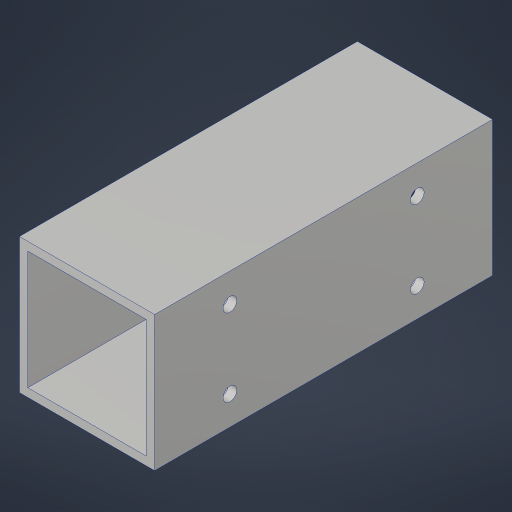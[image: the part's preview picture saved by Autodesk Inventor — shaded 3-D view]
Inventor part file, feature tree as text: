
AUTODESK INVENTOR PART (.ipt)
format: ipt  version: 2023.4 (Build 274418000, 418)  size: 167,424 bytes
history: native  units: in
note: dims shown in document units (in); Inventor stores cm internally (conversion verified against a paired STEP export)
features: extrude x1, hole x1, sketch x1, projected_geometry x1
ambient origin geometry x8: Origin, YZ Plane, XZ Plane, XY Plane, X Axis, Y Axis, Z Axis, Center Point
bodies: Solid1 (feature_tree)
feature tree (4):
  extrude  "Extrusion1"  Depth=3.0in
  hole  "Hole1"  [1 undecoded]
  sketch  "Sketch2"  dims[d4=0.0in d5=3.0in d6=3.1496in d8=360.0deg d10=0.201in d11=0.75in d12=0.385in d13=0.25in d14=0.5635in d15=1.0in d16=0.8108in]
  projected_geometry  "Project Cut Edges1"
note: 1 required parameter value undecoded (feature->parameter linkage not recoverable at this tier; creation-order binding heuristic only, values carry confidence <= 0.55)
